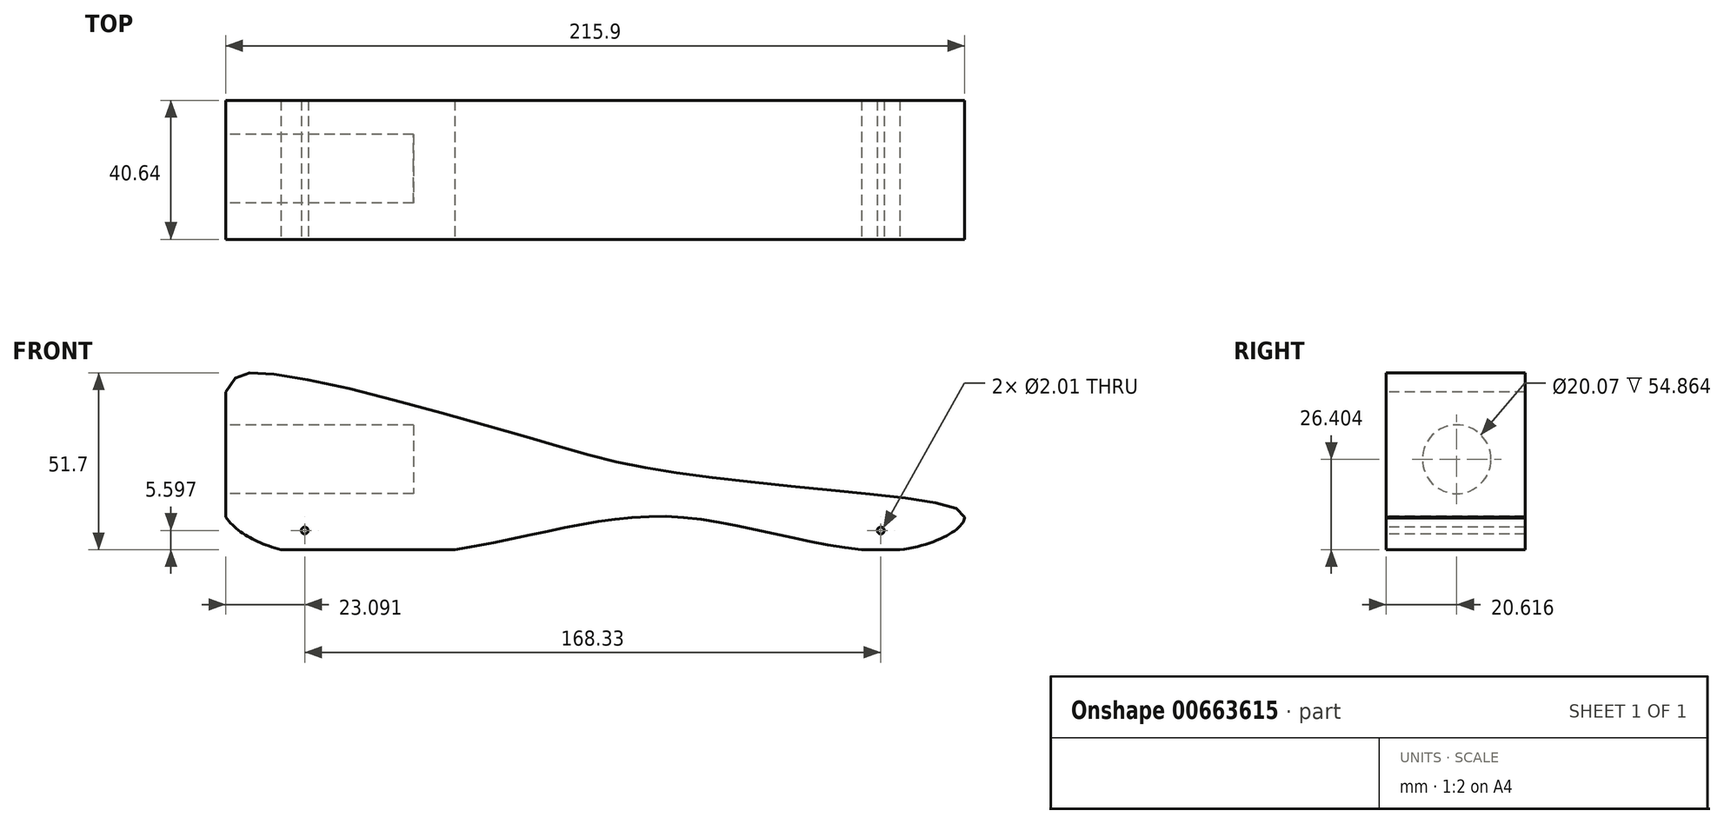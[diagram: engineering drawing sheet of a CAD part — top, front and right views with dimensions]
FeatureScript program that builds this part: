
annotation { "Feature Type Name" : "Feature", "Feature Type Description" : "" }
export const myFeature = defineFeature(function(context is Context, id is Id, definition is map)
    precondition{}
    {
        {
            var Q0;
            Q0=qCreatedBy(makeId("Front.planeOp"),FACE);
            var sketch = newSketch(context, id + "F0", { "sketchPlane" : qUnion([Q0])});
            skLineSegment(sketch, "E0", {"start": v(0, 0) * mm, "end": v(215.9, 0) * mm});
            skLineSegment(sketch, "E1", {"start": v(215.9, 0) * mm, "end": v(215.9, 19.05) * mm});
            skLineSegment(sketch, "E2", {"start": v(215.9, 19.05) * mm, "end": v(0, 63.5) * mm});
            skLineSegment(sketch, "E3", {"start": v(0, 63.5) * mm, "end": v(0, 0) * mm});
            skSolve(sketch);
        }
        {
            var Q0;
            Q0=makeQuery(id+"F0.imprint","IMPRINT",FACE,{"disambiguationData":[TD([[makeQuery(id+"F0.imprint","IMPRINT",EDGE,{"derivedFrom":sQuery(id+"F0.wireOp",EDGE,"E0")}),1.0]])]});
            extrude(context, id + "F1", {"entities" : qUnion([Q0]), "oppositeDirection" : true, "depth" : 40.64 * mm, "offsetDistance" : 25.4 * mm});
        }
        {
            var Q0;
            Q0=makeQuery(id+"F1.opExtrude","SWEPT_FACE",FACE,{"disambiguationData":[OSD([sQuery(id+"F0.wireOp",EDGE,"E3")])]});
            var sketch = newSketch(context, id + "F2", { "sketchPlane" : qUnion([Q0])});
            skCircle(sketch, "E4", {"center": v(-20.62, 26.4) * mm, "radius": 10.03 * mm});
            skSolve(sketch);
        }
        {
            var Q0;
            Q0=makeQuery(id+"F2.imprint","IMPRINT",FACE,{"disambiguationData":[TD([[makeQuery(id+"F2.imprint","IMPRINT",EDGE,{"derivedFrom":sQuery(id+"F2.wireOp",EDGE,"E4")}),1.0]])]});
            extrude(context, id + "F3", {"entities" : qUnion([Q0]), "operationType" : NewBodyOperationType.REMOVE, "oppositeDirection" : true, "depth" : 54.86 * mm, "offsetDistance" : 25.4 * mm});
        }
        {
            var Q0;
            Q0=makeQuery(id+"F1.opExtrude","CAP_FACE",FACE,{"disambiguationData":[OSD([sQuery(id+"F0.wireOp",EDGE,"E0"),sQuery(id+"F0.wireOp",EDGE,"E1"),sQuery(id+"F0.wireOp",EDGE,"E2"),sQuery(id+"F0.wireOp",EDGE,"E3")])],"isStart":true});
            var sketch = newSketch(context, id + "F4", { "sketchPlane" : qUnion([Q0])});
            skPoint(sketch, "E5.7.internal.snap0", {"position": v(215.9, 9.53) * mm});
            skPoint(sketch, "E5.9.internal.snap0", {"position": v(215.9, 9.53) * mm});
            skFitSpline(sketch, "E5", {"points": [v(0, 46.1) * mm, v(9.53, 51.69) * mm, v(86.23, 33.4) * mm, v(128.14, 22.99) * mm, v(193.93, 15.62) * mm, v(215.9, 9.52) * mm, v(196.98, 0) * mm, v(132.46, 9.52) * mm, v(66.93, 0) * mm, v(0, 9.52) * mm, v(0, 46.1) * mm]});
            skSolve(sketch);
        }
        {
            var Q0;
            {var subQ0=sQuery(id+"F4.wireOp",EDGE,"E5");var subQ1=makeQuery(id+"F1.opExtrude","CAP_EDGE",EDGE,{"disambiguationData":[OSD([sQuery(id+"F0.wireOp",EDGE,"E0")])],"isStart":true});var subQ2=makeQuery(id+"F4.imprint","INTERSECT",VERTEX,{"disambiguationData":[OD(3.0)],"derivedFrom":[subQ1,subQ0]});Q0=makeQuery(id+"F4.imprint","IMPRINT",FACE,{"disambiguationData":[TD([[makeQuery(id+"F4.imprint","IMPRINT",EDGE,{"disambiguationData":[TD([[subQ2,-1.0]])],"derivedFrom":subQ0}),1.0]])]});}
            var Q1;
            {var subQ5=makeQuery(id+"F1.opExtrude","CAP_EDGE",EDGE,{"disambiguationData":[OSD([sQuery(id+"F0.wireOp",EDGE,"E2")])],"isStart":true});Q1=makeQuery(id+"F4.imprint","IMPRINT",FACE,{"disambiguationData":[TD([[makeQuery(id+"F4.imprint","IMPRINT",EDGE,{"derivedFrom":subQ5}),1.0]])]});}
            var Q2;
            {var subQ0=sQuery(id+"F4.wireOp",EDGE,"E5");var subQ1=makeQuery(id+"F1.opExtrude","CAP_EDGE",EDGE,{"disambiguationData":[OSD([sQuery(id+"F0.wireOp",EDGE,"E0")])],"isStart":true});var subQ2=makeQuery(id+"F4.imprint","INTERSECT",VERTEX,{"disambiguationData":[OD(1.0)],"derivedFrom":[subQ1,subQ0]});Q2=makeQuery(id+"F4.imprint","IMPRINT",FACE,{"disambiguationData":[TD([[makeQuery(id+"F4.imprint","IMPRINT",EDGE,{"disambiguationData":[TD([[subQ2,-1.0]])],"derivedFrom":subQ0}),1.0]])]});}
            var Q3;
            {var subQ0=sQuery(id+"F4.wireOp",EDGE,"E5");var subQ1=makeQuery(id+"F1.opExtrude","CAP_EDGE",EDGE,{"disambiguationData":[OSD([sQuery(id+"F0.wireOp",EDGE,"E1")])],"isStart":true});var subQ2=makeQuery(id+"F4.imprint","INTERSECT",VERTEX,{"disambiguationData":[OD(1.0)],"derivedFrom":[subQ1,subQ0]});Q3=makeQuery(id+"F4.imprint","IMPRINT",FACE,{"disambiguationData":[TD([[makeQuery(id+"F4.imprint","IMPRINT",EDGE,{"disambiguationData":[TD([[subQ2,-1.0]])],"derivedFrom":subQ0}),1.0]])]});}
            extrude(context, id + "F5", {"entities" : qUnion([Q0, Q1, Q2, Q3]), "operationType" : NewBodyOperationType.REMOVE, "oppositeDirection" : true, "depth" : 50.8 * mm, "offsetDistance" : 25.4 * mm});
        }
        {
            var Q0;
            Q0=makeQuery(id+"F1.opExtrude","CAP_FACE",FACE,{"disambiguationData":[OSD([sQuery(id+"F0.wireOp",EDGE,"E0"),sQuery(id+"F0.wireOp",EDGE,"E1"),sQuery(id+"F0.wireOp",EDGE,"E2"),sQuery(id+"F0.wireOp",EDGE,"E3")])],"isStart":true});
            var sketch = newSketch(context, id + "F6", { "sketchPlane" : qUnion([Q0])});
            skCircle(sketch, "E6", {"center": v(191.42, 5.6) * mm, "radius": 1 * mm});
            skCircle(sketch, "E7", {"center": v(23.1, 5.6) * mm, "radius": 1 * mm});
            skSolve(sketch);
        }
        {
            var Q0;
            Q0=makeQuery(id+"F6.imprint","IMPRINT",FACE,{"disambiguationData":[TD([[makeQuery(id+"F6.imprint","IMPRINT",EDGE,{"derivedFrom":sQuery(id+"F6.wireOp",EDGE,"E7")}),1.0]])]});
            var Q1;
            Q1=makeQuery(id+"F6.imprint","IMPRINT",FACE,{"disambiguationData":[TD([[makeQuery(id+"F6.imprint","IMPRINT",EDGE,{"derivedFrom":sQuery(id+"F6.wireOp",EDGE,"E6")}),1.0]])]});
            extrude(context, id + "F7", {"entities" : qUnion([Q0, Q1]), "operationType" : NewBodyOperationType.REMOVE, "oppositeDirection" : true, "depth" : 50.8 * mm, "offsetDistance" : 25.4 * mm});
        }
    });
